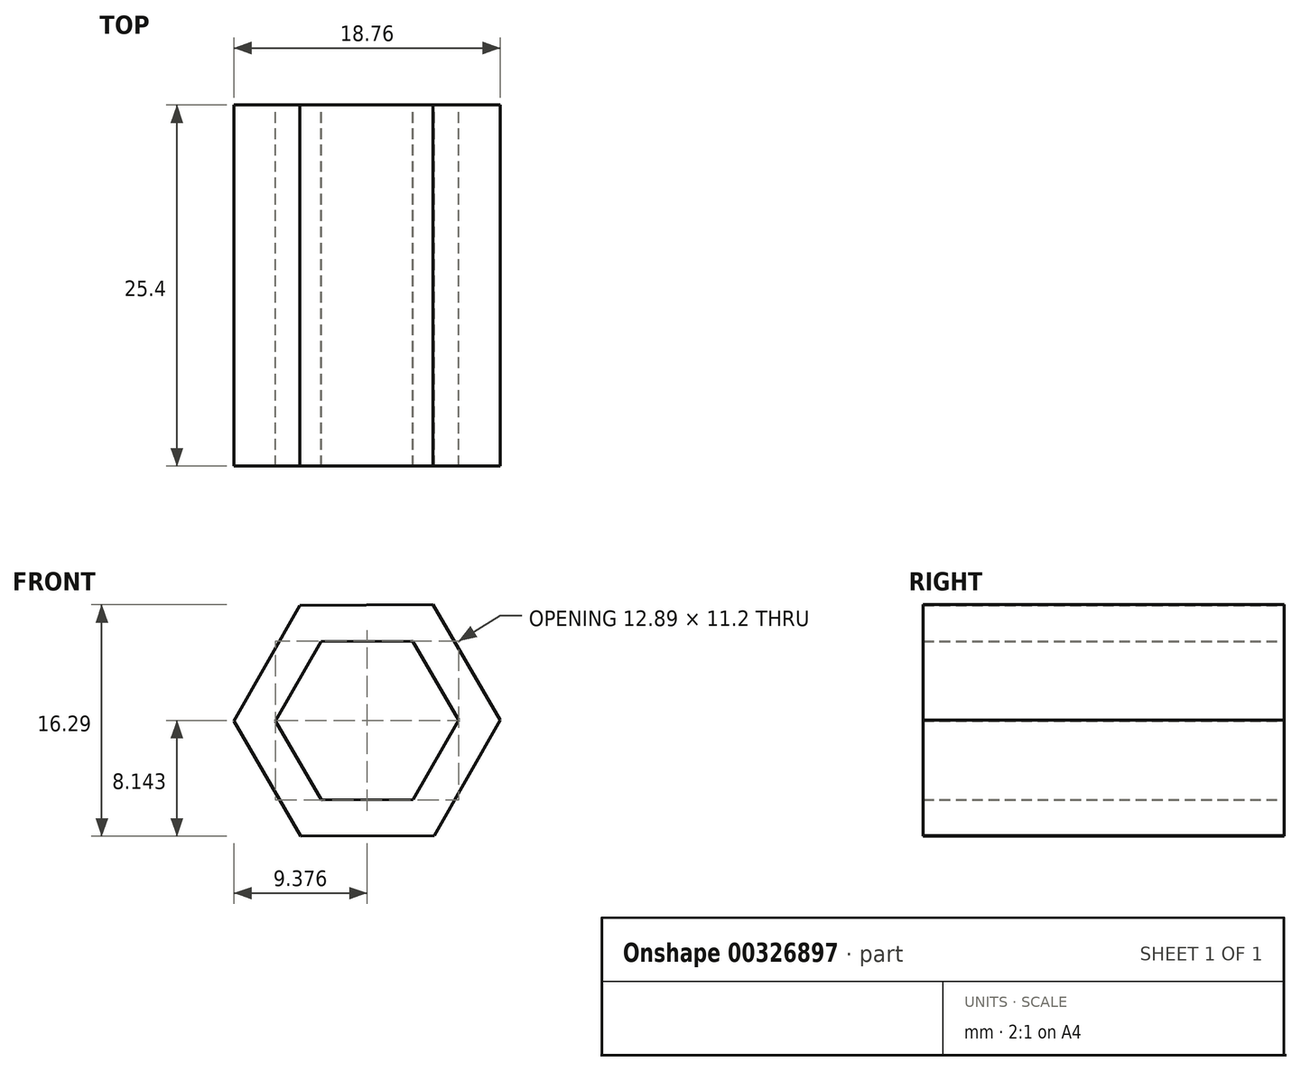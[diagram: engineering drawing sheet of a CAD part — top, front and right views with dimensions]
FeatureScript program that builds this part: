
annotation { "Feature Type Name" : "Feature", "Feature Type Description" : "" }
export const myFeature = defineFeature(function(context is Context, id is Id, definition is map)
    precondition{}
    {
        {
            var Q0;
            Q0=qCreatedBy(makeId("Front.planeOp"),FACE);
            var sketch = newSketch(context, id + "F0", { "sketchPlane" : qUnion([Q0])});
            skCircle(sketch, "E0.cCircle", {"center": v(-30.38, 38.82) * mm, "radius": 9.38 * mm, "construction": true});
            skLineSegment(sketch, "E0.0", {"start": v(-35.1, 46.93) * mm, "end": v(-25.73, 46.97) * mm});
            skLineSegment(sketch, "E0.1", {"start": v(-25.73, 46.97) * mm, "end": v(-21, 38.87) * mm});
            skLineSegment(sketch, "E0.2", {"start": v(-21, 38.87) * mm, "end": v(-25.66, 30.72) * mm});
            skLineSegment(sketch, "E0.3", {"start": v(-25.66, 30.72) * mm, "end": v(-35.04, 30.68) * mm});
            skLineSegment(sketch, "E0.4", {"start": v(-35.04, 30.68) * mm, "end": v(-39.76, 38.78) * mm});
            skLineSegment(sketch, "E0.5", {"start": v(-39.76, 38.78) * mm, "end": v(-35.1, 46.93) * mm});
            skSolve(sketch);
        }
        {
            var Q0;
            Q0=qCreatedBy(makeId("Front.planeOp"),FACE);
            var sketch = newSketch(context, id + "F1", { "sketchPlane" : qUnion([Q0])});
            skCircle(sketch, "E1", {"center": v(-30.72, 39.16) * mm, "radius": 15.2 * mm});
            skPoint(sketch, "E1.first.point", {"position": v(-31.06, 54.35) * mm});
            skPoint(sketch, "E1.second.point", {"position": v(-30.38, 23.97) * mm});
            skPoint(sketch, "E1.third.point", {"position": v(-15.53, 38.82) * mm});
            skSolve(sketch);
        }
        {
            var Q0;
            Q0=makeQuery(id+"F0.imprint","IMPRINT",FACE,{"disambiguationData":[TD([[makeQuery(id+"F0.imprint","IMPRINT",EDGE,{"derivedFrom":sQuery(id+"F0.wireOp",EDGE,"E0.0")}),-1.0]])]});
            var Q1;
            Q1=makeQuery(id+"F1.imprint","IMPRINT",FACE,{"disambiguationData":[TD([[makeQuery(id+"F1.imprint","IMPRINT",EDGE,{"derivedFrom":sQuery(id+"F1.wireOp",EDGE,"E1")}),1.0]])]});
            extrude(context, id + "F2", {"entities" : qUnion([Q0, Q1]), "depth" : 25.4 * mm});
        }
        {
            var Q0;
            Q0 = qSketchRegion(id + "F0", true);
            extrude(context, id + "F3", {"entities" : qUnion([Q0]), "depth" : 25.4 * mm});
        }
        {
            var Q0;
            Q0=makeQuery(id+"F2.opExtrude","SWEPT_BODY",BODY,{"disambiguationData":[OSD([sQuery(id+"F1.wireOp",EDGE,"E1")])]});
            var Q1;
            Q1=makeQuery(id+"F2.opExtrude","SWEPT_BODY",BODY,{"disambiguationData":[OSD([sQuery(id+"F0.wireOp",EDGE,"E0.0"),sQuery(id+"F0.wireOp",EDGE,"E0.1"),sQuery(id+"F0.wireOp",EDGE,"E0.2"),sQuery(id+"F0.wireOp",EDGE,"E0.3"),sQuery(id+"F0.wireOp",EDGE,"E0.4"),sQuery(id+"F0.wireOp",EDGE,"E0.5")])]});
            booleanBodies(context, id + "F4", {"operationType" : BooleanOperationType.INTERSECTION, "tools" : qUnion([Q0, Q1])});
        }
        {
            var Q0;
            Q0=makeQuery(id+"F2.opExtrude","CAP_FACE",FACE,{"disambiguationData":[OSD([sQuery(id+"F1.wireOp",EDGE,"E1")])],"isStart":true});
            var Q1;
            Q1=makeQuery(id+"F2.opExtrude","CAP_FACE",FACE,{"disambiguationData":[OSD([sQuery(id+"F1.wireOp",EDGE,"E1")])],"isStart":false});
            shell(context, id + "F5", {"entities" : qUnion([Q0, Q1]), "thickness" : 2.54 * mm});
        }
    });
